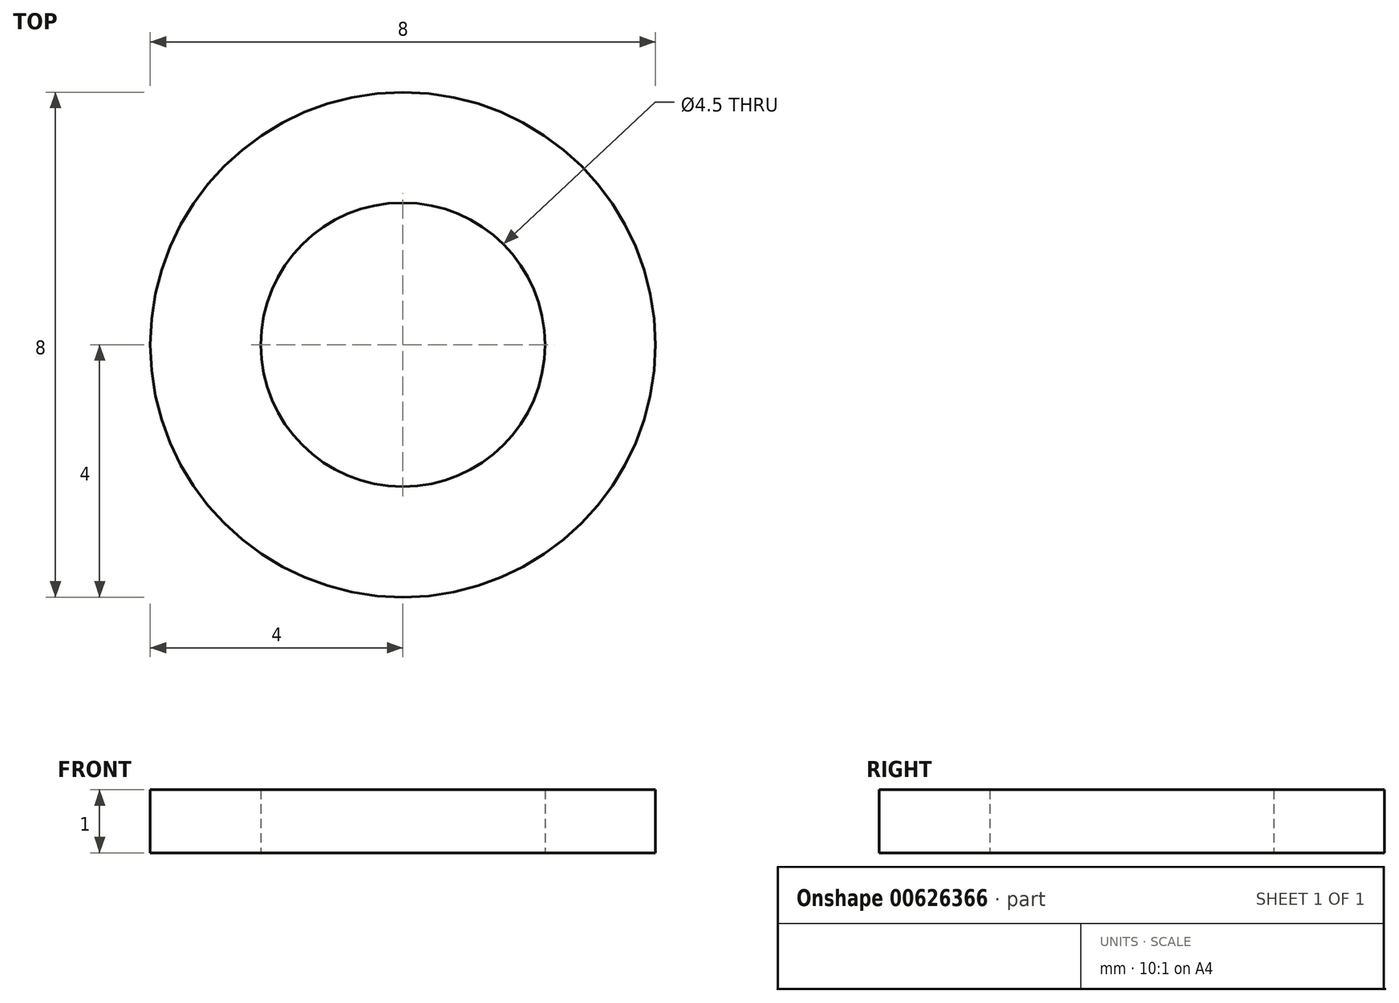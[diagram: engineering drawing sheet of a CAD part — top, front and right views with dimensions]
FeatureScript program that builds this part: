
annotation { "Feature Type Name" : "Feature", "Feature Type Description" : "" }
export const myFeature = defineFeature(function(context is Context, id is Id, definition is map)
    precondition{}
    {
        {
            var Q0;
            Q0=qCreatedBy(makeId("Top.planeOp"),FACE);
            var sketch = newSketch(context, id + "F0", { "sketchPlane" : qUnion([Q0])});
            skCircle(sketch, "E0", {"center": v(0, 0) * mm, "radius": 4 * mm});
            skCircle(sketch, "E1", {"center": v(0, 0) * mm, "radius": 2.25 * mm});
            skSolve(sketch);
        }
        {
            var Q0;
            Q0 = qSketchRegion(id + "F0", true);
            extrude(context, id + "F1", {"entities" : qUnion([Q0]), "depth" : 1 * mm, "offsetDistance" : 25 * mm});
        }
    });
